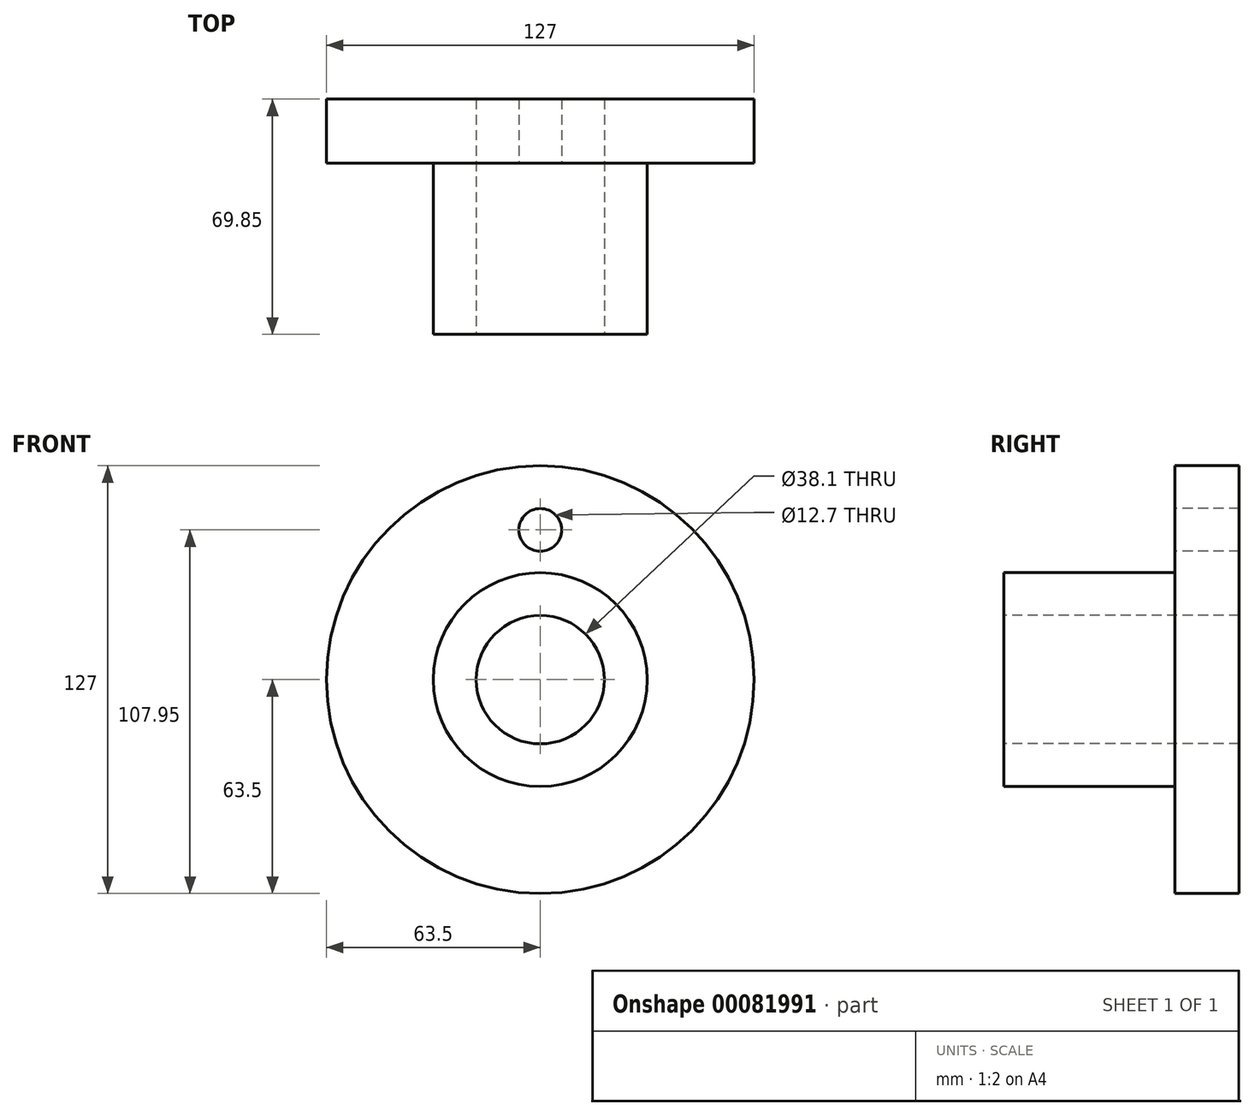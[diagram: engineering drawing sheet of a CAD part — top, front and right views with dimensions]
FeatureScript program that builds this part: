
annotation { "Feature Type Name" : "Feature", "Feature Type Description" : "" }
export const myFeature = defineFeature(function(context is Context, id is Id, definition is map)
    precondition{}
    {
        {
            var Q0;
            Q0=qCreatedBy(makeId("Front.planeOp"),FACE);
            var sketch = newSketch(context, id + "F0", { "sketchPlane" : qUnion([Q0])});
            skCircle(sketch, "E0", {"center": v(0, 0) * mm, "radius": 63.5 * mm});
            skSolve(sketch);
        }
        {
            var Q0;
            Q0 = qSketchRegion(id + "F0", true);
            extrude(context, id + "F1", {"entities" : qUnion([Q0]), "depth" : 19.05 * mm});
        }
        {
            var Q0;
            Q0=qCreatedBy(makeId("Front.planeOp"),FACE);
            cPlane(context, id + "F2", {"entities" : qUnion([Q0]), "cplaneType" : CPlaneType.OFFSET, "offset" : 69.85 * mm, "width" : 152.4 * mm, "height" : 152.4 * mm});
        }
        {
            var Q0;
            Q0=qCreatedBy(id+"F2.planeOp",FACE);
            var sketch = newSketch(context, id + "F3", { "sketchPlane" : qUnion([Q0])});
            skCircle(sketch, "E1", {"center": v(0, 0) * mm, "radius": 31.75 * mm});
            skSolve(sketch);
        }
        {
            var Q0;
            Q0 = qSketchRegion(id + "F3", true);
            extrude(context, id + "F4", {"entities" : qUnion([Q0]), "operationType" : NewBodyOperationType.ADD, "endBound" : BoundingType.UP_TO_NEXT, "oppositeDirection" : true, "depth" : 25.4 * mm});
        }
        {
            var Q0;
            Q0=makeQuery(id+"F4.opExtrude","CAP_FACE",FACE,{"disambiguationData":[OSD([sQuery(id+"F3.wireOp",EDGE,"E1")])],"isStart":true});
            var sketch = newSketch(context, id + "F5", { "sketchPlane" : qUnion([Q0])});
            skCircle(sketch, "E2", {"center": v(0, 0) * mm, "radius": 19.05 * mm});
            skSolve(sketch);
        }
        {
            var Q0;
            Q0 = qSketchRegion(id + "F5", true);
            extrude(context, id + "F6", {"entities" : qUnion([Q0]), "operationType" : NewBodyOperationType.REMOVE, "endBound" : BoundingType.THROUGH_ALL, "oppositeDirection" : true, "depth" : 25.4 * mm});
        }
        {
            var Q0;
            Q0=makeQuery(id+"F1.opExtrude","CAP_FACE",FACE,{"disambiguationData":[OSD([sQuery(id+"F0.wireOp",EDGE,"E0")])],"isStart":false});
            var sketch = newSketch(context, id + "F7", { "sketchPlane" : qUnion([Q0])});
            skCircle(sketch, "E3", {"center": v(0, 0) * mm, "radius": 44.45 * mm, "construction": true});
            skCircle(sketch, "E4", {"center": v(0, 44.45) * mm, "radius": 6.35 * mm});
            skSolve(sketch);
        }
        {
            var Q0;
            Q0 = qSketchRegion(id + "F7", true);
            extrude(context, id + "F8", {"entities" : qUnion([Q0]), "operationType" : NewBodyOperationType.REMOVE, "endBound" : BoundingType.THROUGH_ALL, "oppositeDirection" : true, "depth" : 25.4 * mm});
        }
    });
